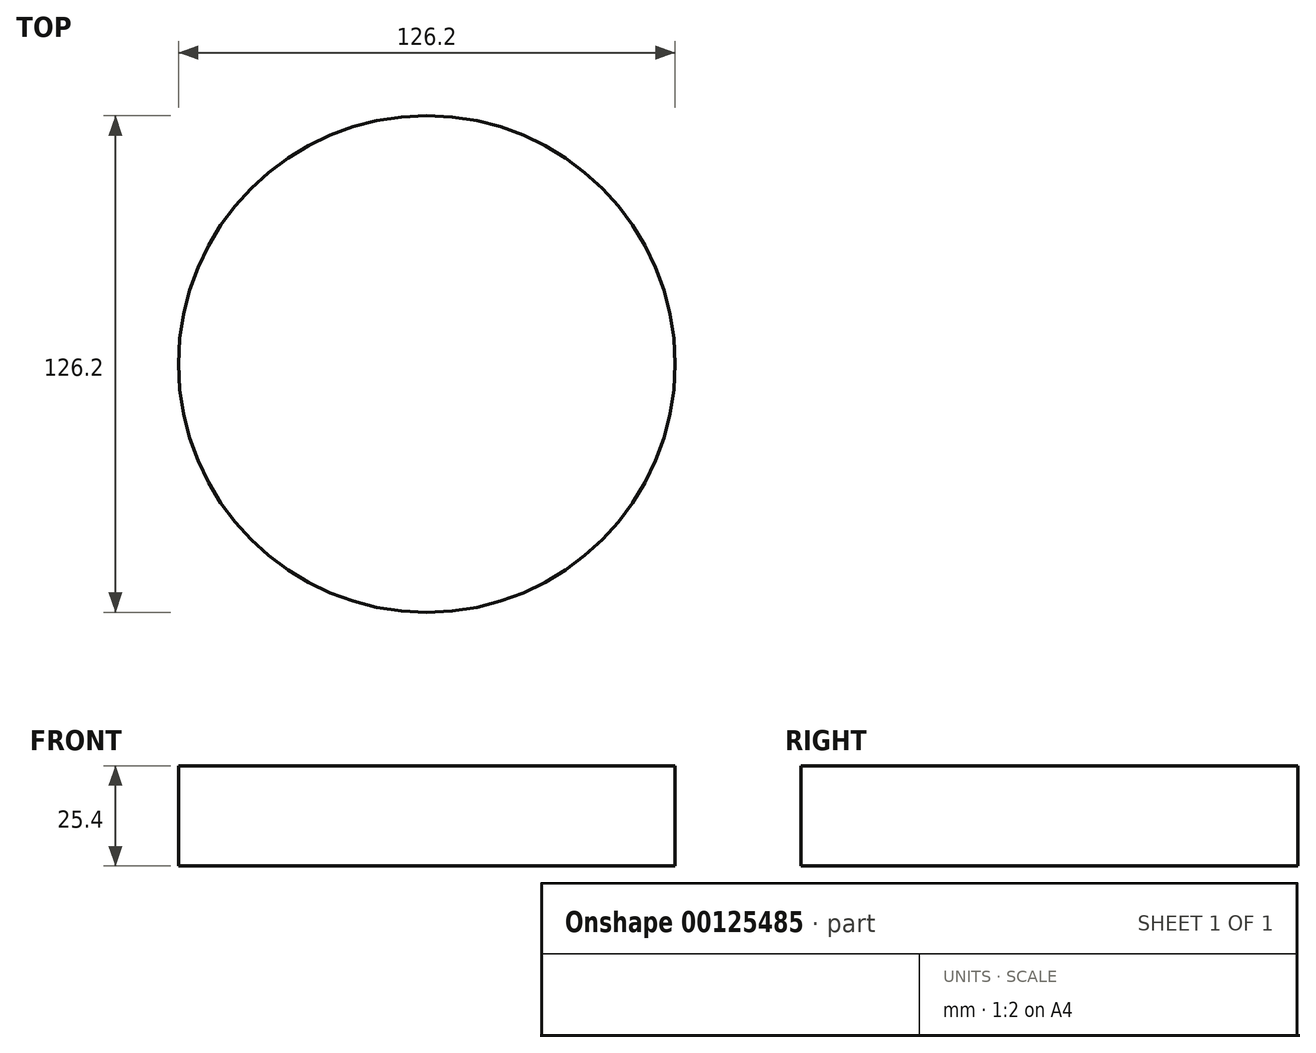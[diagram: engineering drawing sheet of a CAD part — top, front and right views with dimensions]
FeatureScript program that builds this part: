
annotation { "Feature Type Name" : "Feature", "Feature Type Description" : "" }
export const myFeature = defineFeature(function(context is Context, id is Id, definition is map)
    precondition{}
    {
        {
            var Q0;
            Q0=qCreatedBy(makeId("Top.planeOp"),FACE);
            var sketch = newSketch(context, id + "F0", { "sketchPlane" : qUnion([Q0])});
            skCircle(sketch, "E0", {"center": v(0, 0) * mm, "radius": 63.1 * mm});
            skSolve(sketch);
        }
        {
            var Q0;
            Q0=makeQuery(id+"F0.imprint","IMPRINT",FACE,{"disambiguationData":[TD([[makeQuery(id+"F0.imprint","IMPRINT",EDGE,{"derivedFrom":sQuery(id+"F0.wireOp",EDGE,"E0")}),1.0]])]});
            extrude(context, id + "F1", {"entities" : qUnion([Q0]), "depth" : 25.4 * mm});
        }
    });
